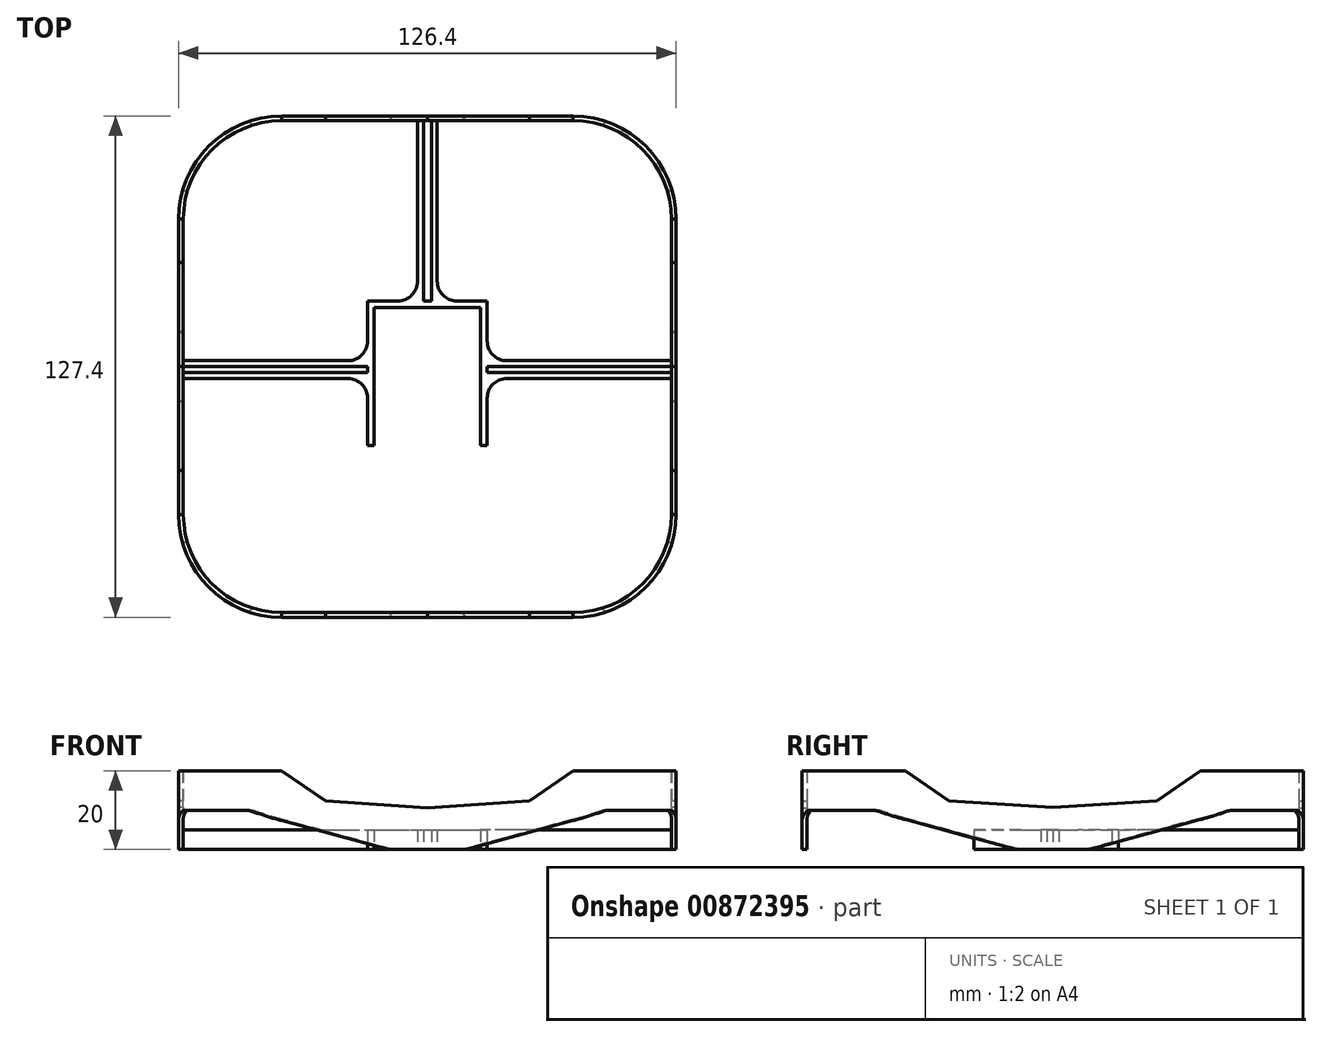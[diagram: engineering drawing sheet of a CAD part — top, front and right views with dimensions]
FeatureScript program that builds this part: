
annotation { "Feature Type Name" : "Feature", "Feature Type Description" : "" }
export const myFeature = defineFeature(function(context is Context, id is Id, definition is map)
    precondition{}
    {
        {
            var Q0;
            Q0=qCreatedBy(makeId("Top.planeOp"),FACE);
            var sketch = newSketch(context, id + "F0", { "sketchPlane" : qUnion([Q0])});
            skLineSegment(sketch, "E0.bottom", {"start": v(-37, 62.5) * mm, "end": v(37, 62.5) * mm});
            skLineSegment(sketch, "E0.top", {"start": v(-37, -62.5) * mm, "end": v(37, -62.5) * mm});
            skLineSegment(sketch, "E0.left", {"start": v(-62, 37.5) * mm, "end": v(-62, -37.5) * mm});
            skLineSegment(sketch, "E0.right", {"start": v(62, 37.5) * mm, "end": v(62, -37.5) * mm});
            skLineSegment(sketch, "E1", {"start": v(0, 0) * mm, "end": v(0, 62.5) * mm, "construction": true});
            skLineSegment(sketch, "E2", {"start": v(0, 0) * mm, "end": v(-62, 0) * mm, "construction": true});
            skLineSegment(sketch, "E3.bottom", {"start": v(-13.5, 15) * mm, "end": v(13.5, 15) * mm});
            skLineSegment(sketch, "E3.top", {"start": v(-13.5, -15) * mm, "end": v(13.5, -15) * mm});
            skLineSegment(sketch, "E3.left", {"start": v(-13.5, 15) * mm, "end": v(-13.5, -15) * mm});
            skLineSegment(sketch, "E3.right", {"start": v(13.5, 15) * mm, "end": v(13.5, -15) * mm});
            skLineSegment(sketch, "E4", {"start": v(0, 15) * mm, "end": v(0, -15) * mm, "construction": true});
            skPoint(sketch, "E5.visualSharp", {"position": v(-62, 62.5) * mm});
            skArc(sketch, "E5.filletArc", {"start": v(-37, 62.5) * mm, "mid": v(-54.68, 55.18) * mm, "end": v(-62, 37.5) * mm});
            skPoint(sketch, "E6.visualSharp", {"position": v(-62, -62.5) * mm});
            skArc(sketch, "E6.filletArc", {"start": v(-62, -37.5) * mm, "mid": v(-54.68, -55.18) * mm, "end": v(-37, -62.5) * mm});
            skPoint(sketch, "E7.visualSharp", {"position": v(62, -62.5) * mm});
            skArc(sketch, "E7.filletArc", {"start": v(37, -62.5) * mm, "mid": v(54.68, -55.18) * mm, "end": v(62, -37.5) * mm});
            skPoint(sketch, "E8.visualSharp", {"position": v(62, 62.5) * mm});
            skArc(sketch, "E8.filletArc", {"start": v(62, 37.5) * mm, "mid": v(54.68, 55.18) * mm, "end": v(37, 62.5) * mm});
            skArc(sketch, "E9.0", {"start": v(-37, 63.7) * mm, "mid": v(-55.53, 56.03) * mm, "end": v(-63.2, 37.5) * mm});
            skLineSegment(sketch, "E9.1", {"start": v(-63.2, 37.5) * mm, "end": v(-63.2, -37.5) * mm});
            skLineSegment(sketch, "E9.2", {"start": v(-37, 63.7) * mm, "end": v(37, 63.7) * mm});
            skArc(sketch, "E9.3", {"start": v(-63.2, -37.5) * mm, "mid": v(-55.53, -56.03) * mm, "end": v(-37, -63.7) * mm});
            skArc(sketch, "E9.4", {"start": v(63.2, 37.5) * mm, "mid": v(55.53, 56.03) * mm, "end": v(37, 63.7) * mm});
            skLineSegment(sketch, "E9.5", {"start": v(63.2, 37.5) * mm, "end": v(63.2, -37.5) * mm});
            skArc(sketch, "E9.6", {"start": v(37, -63.7) * mm, "mid": v(55.53, -56.03) * mm, "end": v(63.2, -37.5) * mm});
            skLineSegment(sketch, "E9.7", {"start": v(-37, -63.7) * mm, "end": v(37, -63.7) * mm});
            skLineSegment(sketch, "E10.0", {"start": v(15.2, 16.7) * mm, "end": v(15.2, -15) * mm});
            skLineSegment(sketch, "E10.1", {"start": v(-15.2, 16.7) * mm, "end": v(15.2, 16.7) * mm});
            skLineSegment(sketch, "E10.2", {"start": v(-15.2, 16.7) * mm, "end": v(-15.2, -16.7) * mm});
            skLineSegment(sketch, "E11.bottom", {"start": v(1, 62.5) * mm, "end": v(2.5, 62.5) * mm});
            skLineSegment(sketch, "E11.top", {"start": v(1, 16.7) * mm, "end": v(2.5, 16.7) * mm});
            skLineSegment(sketch, "E11.left", {"start": v(1, 62.5) * mm, "end": v(1, 16.7) * mm});
            skLineSegment(sketch, "E11.right", {"start": v(2.5, 62.5) * mm, "end": v(2.5, 16.7) * mm});
            skLineSegment(sketch, "E12.bottom", {"start": v(-2.5, 62.5) * mm, "end": v(-1, 62.5) * mm});
            skLineSegment(sketch, "E12.top", {"start": v(-2.5, 16.7) * mm, "end": v(-1, 16.7) * mm});
            skLineSegment(sketch, "E12.left", {"start": v(-2.5, 62.5) * mm, "end": v(-2.5, 16.7) * mm});
            skLineSegment(sketch, "E12.right", {"start": v(-1, 62.5) * mm, "end": v(-1, 16.7) * mm});
            skLineSegment(sketch, "E13.bottom", {"start": v(-62, 1.5) * mm, "end": v(-15.2, 1.5) * mm});
            skLineSegment(sketch, "E13.top", {"start": v(-62, 0) * mm, "end": v(-15.2, 0) * mm});
            skLineSegment(sketch, "E13.left", {"start": v(-62, 1.5) * mm, "end": v(-62, 0) * mm});
            skLineSegment(sketch, "E13.right", {"start": v(-15.2, 1.5) * mm, "end": v(-15.2, 0) * mm});
            skLineSegment(sketch, "E14.bottom", {"start": v(-62, -1.5) * mm, "end": v(-15.2, -1.5) * mm});
            skLineSegment(sketch, "E14.top", {"start": v(-62, -3) * mm, "end": v(-15.2, -3) * mm});
            skLineSegment(sketch, "E14.left", {"start": v(-62, -1.5) * mm, "end": v(-62, -3) * mm});
            skLineSegment(sketch, "E14.right", {"start": v(-15.2, -1.5) * mm, "end": v(-15.2, -3) * mm});
            skLineSegment(sketch, "E15.MirrorCS", {"start": v(62, -3) * mm, "end": v(15.2, -3) * mm});
            skLineSegment(sketch, "E16.MirrorCS", {"start": v(62, -1.5) * mm, "end": v(15.2, -1.5) * mm});
            skLineSegment(sketch, "E17.MirrorCS", {"start": v(62, 0) * mm, "end": v(15.2, 0) * mm});
            skLineSegment(sketch, "E18.MirrorCS", {"start": v(62, 1.5) * mm, "end": v(15.2, 1.5) * mm});
            skLineSegment(sketch, "E19", {"start": v(15.2, -15) * mm, "end": v(15.2, -20) * mm});
            skLineSegment(sketch, "E20", {"start": v(15.2, -20) * mm, "end": v(13.5, -20) * mm});
            skLineSegment(sketch, "E21", {"start": v(13.5, -20) * mm, "end": v(13.5, -15) * mm});
            skLineSegment(sketch, "E22", {"start": v(-15.2, -16.7) * mm, "end": v(-15.2, -20) * mm});
            skLineSegment(sketch, "E23", {"start": v(-15.2, -20) * mm, "end": v(-13.5, -20) * mm});
            skLineSegment(sketch, "E24", {"start": v(-13.5, -20) * mm, "end": v(-13.5, -15) * mm});
            skLineSegment(sketch, "E25", {"start": v(0, 0) * mm, "end": v(-7.2, 7.2) * mm, "construction": true});
            skLineSegment(sketch, "E26", {"start": v(0, 0) * mm, "end": v(-6.83, -6.83) * mm, "construction": true});
            skSolve(sketch);
        }
        {
            var Q0;
            Q0=makeQuery(id+"F0.imprint","IMPRINT",FACE,{"disambiguationData":[TD([[makeQuery(id+"F0.imprint","IMPRINT",EDGE,{"derivedFrom":sQuery(id+"F0.wireOp",EDGE,"E0.top")}),-1.0]])]});
            extrude(context, id + "F1", {"entities" : qUnion([Q0]), "depth" : 20 * mm, "offsetDistance" : 25 * mm});
        }
        {
            var Q0;
            {var subQ0=sQuery(id+"F0.wireOp",EDGE,"E11.left");Q0=makeQuery(id+"F0.imprint","IMPRINT",FACE,{"disambiguationData":[TD([[makeQuery(id+"F0.imprint","IMPRINT",EDGE,{"derivedFrom":subQ0}),1.0]])]});}
            var Q1;
            Q1=makeQuery(id+"F0.imprint","IMPRINT",FACE,{"disambiguationData":[TD([[makeQuery(id+"F0.imprint","IMPRINT",EDGE,{"derivedFrom":sQuery(id+"F0.wireOp",EDGE,"E3.bottom")}),1.0]])]});
            var Q2;
            {var subQ2=sQuery(id+"F0.wireOp",EDGE,"E12.left");Q2=makeQuery(id+"F0.imprint","IMPRINT",FACE,{"disambiguationData":[TD([[makeQuery(id+"F0.imprint","IMPRINT",EDGE,{"derivedFrom":subQ2}),1.0]])]});}
            var Q3;
            {var subQ0=sQuery(id+"F0.wireOp",EDGE,"E13.bottom");Q3=makeQuery(id+"F0.imprint","IMPRINT",FACE,{"disambiguationData":[TD([[makeQuery(id+"F0.imprint","IMPRINT",EDGE,{"derivedFrom":subQ0}),-1.0]])]});}
            var Q4;
            {var subQ2=sQuery(id+"F0.wireOp",EDGE,"E14.bottom");Q4=makeQuery(id+"F0.imprint","IMPRINT",FACE,{"disambiguationData":[TD([[makeQuery(id+"F0.imprint","IMPRINT",EDGE,{"derivedFrom":subQ2}),-1.0]])]});}
            var Q5;
            {var subQ0=sQuery(id+"F0.wireOp",EDGE,"E17.MirrorCS");Q5=makeQuery(id+"F0.imprint","IMPRINT",FACE,{"disambiguationData":[TD([[makeQuery(id+"F0.imprint","IMPRINT",EDGE,{"derivedFrom":subQ0}),-1.0]])]});}
            var Q6;
            {var subQ0=sQuery(id+"F0.wireOp",EDGE,"E15.MirrorCS");Q6=makeQuery(id+"F0.imprint","IMPRINT",FACE,{"disambiguationData":[TD([[makeQuery(id+"F0.imprint","IMPRINT",EDGE,{"derivedFrom":subQ0}),-1.0]])]});}
            extrude(context, id + "F2", {"entities" : qUnion([Q0, Q1, Q2, Q3, Q4, Q5, Q6]), "operationType" : NewBodyOperationType.ADD, "depth" : 5 * mm, "offsetDistance" : 25 * mm});
        }
        {
            var Q0;
            Q0=makeQuery(id+"F2.opExtrude","SWEPT_EDGE",EDGE,{"disambiguationData":[OSD([sQuery(id+"F0.wireOp",EDGE,"E0.bottom"),sQuery(id+"F0.wireOp",EDGE,"E12.left")])]});
            var Q1;
            Q1=makeQuery(id+"F2.opExtrude","SWEPT_EDGE",EDGE,{"disambiguationData":[OSD([sQuery(id+"F0.wireOp",EDGE,"E0.bottom"),sQuery(id+"F0.wireOp",EDGE,"E11.right")])]});
            var Q2;
            Q2=makeQuery(id+"F2.opExtrude","SWEPT_EDGE",EDGE,{"disambiguationData":[OSD([sQuery(id+"F0.wireOp",EDGE,"E10.1"),sQuery(id+"F0.wireOp",EDGE,"E12.left")])]});
            var Q3;
            Q3=makeQuery(id+"F2.opExtrude","SWEPT_EDGE",EDGE,{"disambiguationData":[OSD([sQuery(id+"F0.wireOp",EDGE,"E10.1"),sQuery(id+"F0.wireOp",EDGE,"E11.right")])]});
            var Q4;
            Q4=makeQuery(id+"F2.opExtrude","SWEPT_EDGE",EDGE,{"disambiguationData":[OSD([sQuery(id+"F0.wireOp",EDGE,"E0.right"),sQuery(id+"F0.wireOp",EDGE,"E18.MirrorCS")])]});
            var Q5;
            Q5=makeQuery(id+"F2.opExtrude","SWEPT_EDGE",EDGE,{"disambiguationData":[OSD([sQuery(id+"F0.wireOp",EDGE,"E10.0"),sQuery(id+"F0.wireOp",EDGE,"E18.MirrorCS")])]});
            var Q6;
            Q6=makeQuery(id+"F2.opExtrude","SWEPT_EDGE",EDGE,{"disambiguationData":[OSD([sQuery(id+"F0.wireOp",EDGE,"E0.right"),sQuery(id+"F0.wireOp",EDGE,"E15.MirrorCS")])]});
            var Q7;
            Q7=makeQuery(id+"F2.opExtrude","SWEPT_EDGE",EDGE,{"disambiguationData":[OSD([sQuery(id+"F0.wireOp",EDGE,"E10.0"),sQuery(id+"F0.wireOp",EDGE,"E15.MirrorCS")])]});
            var Q8;
            Q8=makeQuery(id+"F2.opExtrude","SWEPT_EDGE",EDGE,{"disambiguationData":[OSD([sQuery(id+"F0.wireOp",EDGE,"E10.2"),sQuery(id+"F0.wireOp",EDGE,"E14.top")])]});
            var Q9;
            Q9=makeQuery(id+"F2.opExtrude","SWEPT_EDGE",EDGE,{"disambiguationData":[OSD([sQuery(id+"F0.wireOp",EDGE,"E0.left"),sQuery(id+"F0.wireOp",EDGE,"E14.top")])]});
            var Q10;
            Q10=makeQuery(id+"F2.opExtrude","SWEPT_EDGE",EDGE,{"disambiguationData":[OSD([sQuery(id+"F0.wireOp",EDGE,"E0.left"),sQuery(id+"F0.wireOp",EDGE,"E13.bottom")])]});
            var Q11;
            Q11=makeQuery(id+"F2.opExtrude","SWEPT_EDGE",EDGE,{"disambiguationData":[OSD([sQuery(id+"F0.wireOp",EDGE,"E10.2"),sQuery(id+"F0.wireOp",EDGE,"E13.bottom")])]});
            var Q12;
            {var subQ0=sQuery(id+"F0.wireOp",EDGE,"E0.bottom");Q12=makeQuery(id+"F2.opExtrude","CAP_EDGE",EDGE,{"disambiguationData":[OSD([subQ0]),TDD([makeQuery(id+"F0.imprint","IMPRINT",EDGE,{"disambiguationData":[TD([[makeQuery(id+"F0.imprint","INTERSECT",VERTEX,{"derivedFrom":[subQ0,sQuery(id+"F0.wireOp",EDGE,"E11.left")]}),-1.0]])],"derivedFrom":subQ0})])],"isStart":false});}
            var Q13;
            {var subQ0=sQuery(id+"F0.wireOp",EDGE,"E0.bottom");Q13=makeQuery(id+"F2.opExtrude","CAP_EDGE",EDGE,{"disambiguationData":[OSD([subQ0]),TDD([makeQuery(id+"F0.imprint","IMPRINT",EDGE,{"disambiguationData":[TD([[makeQuery(id+"F0.imprint","INTERSECT",VERTEX,{"derivedFrom":[subQ0,sQuery(id+"F0.wireOp",EDGE,"E12.right")]}),1.0]])],"derivedFrom":subQ0})])],"isStart":false});}
            var Q14;
            {var subQ0=sQuery(id+"F0.wireOp",EDGE,"E0.right");Q14=makeQuery(id+"F2.opExtrude","CAP_EDGE",EDGE,{"disambiguationData":[OSD([subQ0]),TDD([makeQuery(id+"F0.imprint","IMPRINT",EDGE,{"disambiguationData":[TD([[makeQuery(id+"F0.imprint","INTERSECT",VERTEX,{"derivedFrom":[subQ0,sQuery(id+"F0.wireOp",EDGE,"E17.MirrorCS")]}),1.0]])],"derivedFrom":subQ0})])],"isStart":false});}
            var Q15;
            {var subQ0=sQuery(id+"F0.wireOp",EDGE,"E0.right");Q15=makeQuery(id+"F2.opExtrude","CAP_EDGE",EDGE,{"disambiguationData":[OSD([subQ0]),TDD([makeQuery(id+"F0.imprint","IMPRINT",EDGE,{"disambiguationData":[TD([[makeQuery(id+"F0.imprint","INTERSECT",VERTEX,{"derivedFrom":[subQ0,sQuery(id+"F0.wireOp",EDGE,"E15.MirrorCS")]}),1.0]])],"derivedFrom":subQ0})])],"isStart":false});}
            var Q16;
            {var subQ0=sQuery(id+"F0.wireOp",EDGE,"E0.left");Q16=makeQuery(id+"F2.opExtrude","CAP_EDGE",EDGE,{"disambiguationData":[OSD([subQ0]),TDD([makeQuery(id+"F0.imprint","IMPRINT",EDGE,{"disambiguationData":[TD([[makeQuery(id+"F0.imprint","INTERSECT",VERTEX,{"derivedFrom":[subQ0,sQuery(id+"F0.wireOp",EDGE,"E13.bottom")]}),-1.0]])],"derivedFrom":subQ0})])],"isStart":false});}
            var Q17;
            {var subQ0=sQuery(id+"F0.wireOp",EDGE,"E0.left");Q17=makeQuery(id+"F2.opExtrude","CAP_EDGE",EDGE,{"disambiguationData":[OSD([subQ0]),TDD([makeQuery(id+"F0.imprint","IMPRINT",EDGE,{"disambiguationData":[TD([[makeQuery(id+"F0.imprint","INTERSECT",VERTEX,{"derivedFrom":[subQ0,sQuery(id+"F0.wireOp",EDGE,"E14.top")]}),1.0]])],"derivedFrom":subQ0})])],"isStart":false});}
            fillet(context, id + "F3", {"entities" : qUnion([Q0, Q1, Q2, Q3, Q4, Q5, Q6, Q7, Q8, Q9, Q10, Q11, Q12, Q13, Q14, Q15, Q16, Q17]), "radius" : 5 * mm, "tangentPropagation" : true, "allowEdgeOverflow" : false});
        }
        {
            var Q0;
            Q0=makeQuery(id+"F1.opExtrude","SWEPT_FACE",FACE,{"disambiguationData":[OSD([sQuery(id+"F0.wireOp",EDGE,"E9.2")])]});
            var sketch = newSketch(context, id + "F4", { "sketchPlane" : qUnion([Q0])});
            skLineSegment(sketch, "E27", {"start": v(-37, 20) * mm, "end": v(-25.9, 12.4) * mm});
            skLineSegment(sketch, "E28", {"start": v(-25.9, 12.4) * mm, "end": v(0, 10.65) * mm});
            skLineSegment(sketch, "E29.MirrorCS", {"start": v(37, 20) * mm, "end": v(25.9, 12.4) * mm});
            skLineSegment(sketch, "E30.MirrorCS", {"start": v(25.9, 12.4) * mm, "end": v(0, 10.65) * mm});
            skSolve(sketch);
        }
        {
            var Q0;
            Q0=makeQuery(id+"F4.imprint","IMPRINT",FACE,{"disambiguationData":[TD([[makeQuery(id+"F4.imprint","IMPRINT",EDGE,{"derivedFrom":sQuery(id+"F4.wireOp",EDGE,"E27")}),1.0]])]});
            extrude(context, id + "F5", {"entities" : qUnion([Q0]), "operationType" : NewBodyOperationType.REMOVE, "oppositeDirection" : true, "depth" : 150.7 * mm, "offsetDistance" : 25 * mm});
        }
        {
            var Q0;
            Q0=makeQuery(id+"F1.opExtrude","SWEPT_FACE",FACE,{"disambiguationData":[OSD([sQuery(id+"F0.wireOp",EDGE,"E9.1")])]});
            var sketch = newSketch(context, id + "F6", { "sketchPlane" : qUnion([Q0])});
            skLineSegment(sketch, "E31", {"start": v(-37.5, 20) * mm, "end": v(-26.4, 12.4) * mm});
            skLineSegment(sketch, "E32", {"start": v(-26.4, 12.4) * mm, "end": v(0, 10.68) * mm});
            skLineSegment(sketch, "E33.MirrorCS", {"start": v(26.4, 12.4) * mm, "end": v(0, 10.68) * mm});
            skLineSegment(sketch, "E34.MirrorCS", {"start": v(37.5, 20) * mm, "end": v(26.4, 12.4) * mm});
            skSolve(sketch);
        }
        {
            var Q0;
            Q0=makeQuery(id+"F6.imprint","IMPRINT",FACE,{"disambiguationData":[TD([[makeQuery(id+"F6.imprint","IMPRINT",EDGE,{"derivedFrom":sQuery(id+"F6.wireOp",EDGE,"E31")}),1.0]])]});
            extrude(context, id + "F7", {"entities" : qUnion([Q0]), "operationType" : NewBodyOperationType.REMOVE, "oppositeDirection" : true, "depth" : 137.6 * mm, "offsetDistance" : 25 * mm});
        }
        {
            var Q0;
            Q0=sQuery(id+"F0.wireOp",EDGE,"E25");
            cPlane(context, id + "F8", {"entities" : qUnion([Q0]), "cplaneType" : CPlaneType.LINE_ANGLE, "offset" : 25 * mm, "angle" : 90 * degree, "width" : 150 * mm, "height" : 150 * mm});
        }
        {
            var Q0;
            Q0=qCreatedBy(id+"F8.planeOp",FACE);
            cPlane(context, id + "F9", {"entities" : qUnion([Q0]), "cplaneType" : CPlaneType.OFFSET, "offset" : 101.3 * mm, "width" : 150 * mm, "height" : 150 * mm});
        }
        {
            var Q0;
            Q0=qCreatedBy(id+"F9.planeOp",FACE);
            var sketch = newSketch(context, id + "F10", { "sketchPlane" : qUnion([Q0])});
            skLineSegment(sketch, "E35", {"start": v(0, 0) * mm, "end": v(0, 10) * mm});
            skLineSegment(sketch, "E36", {"start": v(0, 10) * mm, "end": v(-12, 10) * mm});
            skLineSegment(sketch, "E37", {"start": v(-12, 10) * mm, "end": v(-38.04, 0) * mm});
            skLineSegment(sketch, "E38.MirrorCS", {"start": v(0, 10) * mm, "end": v(12, 10) * mm});
            skLineSegment(sketch, "E39.MirrorCS", {"start": v(12, 10) * mm, "end": v(38.04, 0) * mm});
            skLineSegment(sketch, "E40", {"start": v(-38.04, 0) * mm, "end": v(38.04, 0) * mm});
            skSolve(sketch);
        }
        {
            var Q0;
            Q0=qCreatedBy(id+"F8.planeOp",FACE);
            cPlane(context, id + "F11", {"entities" : qUnion([Q0]), "cplaneType" : CPlaneType.OFFSET, "offset" : 105 * mm, "oppositeDirection" : true, "width" : 150 * mm, "height" : 150 * mm});
        }
        {
            var Q0;
            Q0=qCreatedBy(id+"F11.planeOp",FACE);
            var sketch = newSketch(context, id + "F12", { "sketchPlane" : qUnion([Q0])});
            skLineSegment(sketch, "E41.0", {"start": v(-38.04, 0) * mm, "end": v(38.04, 0) * mm});
            skLineSegment(sketch, "E42.0", {"start": v(-12, 10) * mm, "end": v(-38.04, 0) * mm});
            skLineSegment(sketch, "E43.0", {"start": v(12, 10) * mm, "end": v(38.04, 0) * mm});
            skLineSegment(sketch, "E44.0", {"start": v(0, 10) * mm, "end": v(12, 10) * mm});
            skLineSegment(sketch, "E45.0", {"start": v(0, 10) * mm, "end": v(-12, 10) * mm});
            skSolve(sketch);
        }
        {
            var Q0;
            Q0=makeQuery(id+"F12.imprint","IMPRINT",FACE,{"disambiguationData":[TD([[makeQuery(id+"F12.imprint","IMPRINT",EDGE,{"derivedFrom":sQuery(id+"F12.wireOp",EDGE,"E41.0")}),1.0]])]});
            extrude(context, id + "F13", {"entities" : qUnion([Q0]), "operationType" : NewBodyOperationType.REMOVE, "depth" : 60 * mm, "offsetDistance" : 25 * mm});
        }
        {
            var Q0;
            {var subQ0=sQuery(id+"F10.wireOp",EDGE,"E35");Q0=makeQuery(id+"F10.imprint","IMPRINT",FACE,{"disambiguationData":[TD([[makeQuery(id+"F10.imprint","IMPRINT",EDGE,{"derivedFrom":subQ0}),1.0]])]});}
            var Q1;
            {var subQ0=sQuery(id+"F10.wireOp",EDGE,"E35");Q1=makeQuery(id+"F10.imprint","IMPRINT",FACE,{"disambiguationData":[TD([[makeQuery(id+"F10.imprint","IMPRINT",EDGE,{"derivedFrom":subQ0}),-1.0]])]});}
            extrude(context, id + "F14", {"entities" : qUnion([Q0, Q1]), "operationType" : NewBodyOperationType.REMOVE, "oppositeDirection" : true, "depth" : 56.1 * mm, "offsetDistance" : 25 * mm});
        }
        {
            var Q0;
            Q0=sQuery(id+"F0.wireOp",EDGE,"E26");
            cPlane(context, id + "F15", {"entities" : qUnion([Q0]), "cplaneType" : CPlaneType.LINE_ANGLE, "offset" : 25 * mm, "angle" : 90 * degree, "oppositeDirection" : true, "width" : 150 * mm, "height" : 150 * mm});
        }
        {
            var Q0;
            Q0=qCreatedBy(id+"F15.planeOp",FACE);
            cPlane(context, id + "F16", {"entities" : qUnion([Q0]), "cplaneType" : CPlaneType.OFFSET, "offset" : 116 * mm, "width" : 150 * mm, "height" : 150 * mm});
        }
        {
            var Q0;
            Q0=qCreatedBy(id+"F15.planeOp",FACE);
            cPlane(context, id + "F17", {"entities" : qUnion([Q0]), "cplaneType" : CPlaneType.OFFSET, "offset" : 119 * mm, "oppositeDirection" : true, "width" : 150 * mm, "height" : 150 * mm});
        }
        {
            var Q0;
            Q0=qCreatedBy(id+"F16.planeOp",FACE);
            var sketch = newSketch(context, id + "F18", { "sketchPlane" : qUnion([Q0])});
            skPoint(sketch, "E46.0", {"position": v(0, 0) * mm});
            skLineSegment(sketch, "E47.0", {"start": v(-38.04, 0) * mm, "end": v(38.04, 0) * mm});
            skLineSegment(sketch, "E48.0", {"start": v(-12, 10) * mm, "end": v(-38.04, 0) * mm});
            skLineSegment(sketch, "E49.0", {"start": v(12, 10) * mm, "end": v(38.04, 0) * mm});
            skLineSegment(sketch, "E50.0", {"start": v(0, 10) * mm, "end": v(12, 10) * mm});
            skLineSegment(sketch, "E51.0", {"start": v(0, 10) * mm, "end": v(-12, 10) * mm});
            skSolve(sketch);
        }
        {
            var Q0;
            Q0=qCreatedBy(id+"F17.planeOp",FACE);
            var sketch = newSketch(context, id + "F19", { "sketchPlane" : qUnion([Q0])});
            skLineSegment(sketch, "E52.0", {"start": v(-38.04, 0) * mm, "end": v(38.04, 0) * mm});
            skLineSegment(sketch, "E53.0", {"start": v(-12, 10) * mm, "end": v(-38.04, 0) * mm});
            skLineSegment(sketch, "E54.0", {"start": v(0, 10) * mm, "end": v(-12, 10) * mm});
            skLineSegment(sketch, "E55.0", {"start": v(0, 10) * mm, "end": v(12, 10) * mm});
            skLineSegment(sketch, "E56.0", {"start": v(12, 10) * mm, "end": v(38.04, 0) * mm});
            skSolve(sketch);
        }
        {
            var Q0;
            Q0=makeQuery(id+"F19.imprint","IMPRINT",FACE,{"disambiguationData":[TD([[makeQuery(id+"F19.imprint","IMPRINT",EDGE,{"derivedFrom":sQuery(id+"F19.wireOp",EDGE,"E52.0")}),1.0]])]});
            extrude(context, id + "F20", {"entities" : qUnion([Q0]), "operationType" : NewBodyOperationType.REMOVE, "depth" : 72.8 * mm, "offsetDistance" : 25 * mm});
        }
        {
            var Q0;
            Q0=makeQuery(id+"F18.imprint","IMPRINT",FACE,{"disambiguationData":[TD([[makeQuery(id+"F18.imprint","IMPRINT",EDGE,{"derivedFrom":sQuery(id+"F18.wireOp",EDGE,"E47.0")}),1.0]])]});
            extrude(context, id + "F21", {"entities" : qUnion([Q0]), "operationType" : NewBodyOperationType.REMOVE, "oppositeDirection" : true, "depth" : 71.7 * mm, "offsetDistance" : 25 * mm});
        }
    });
